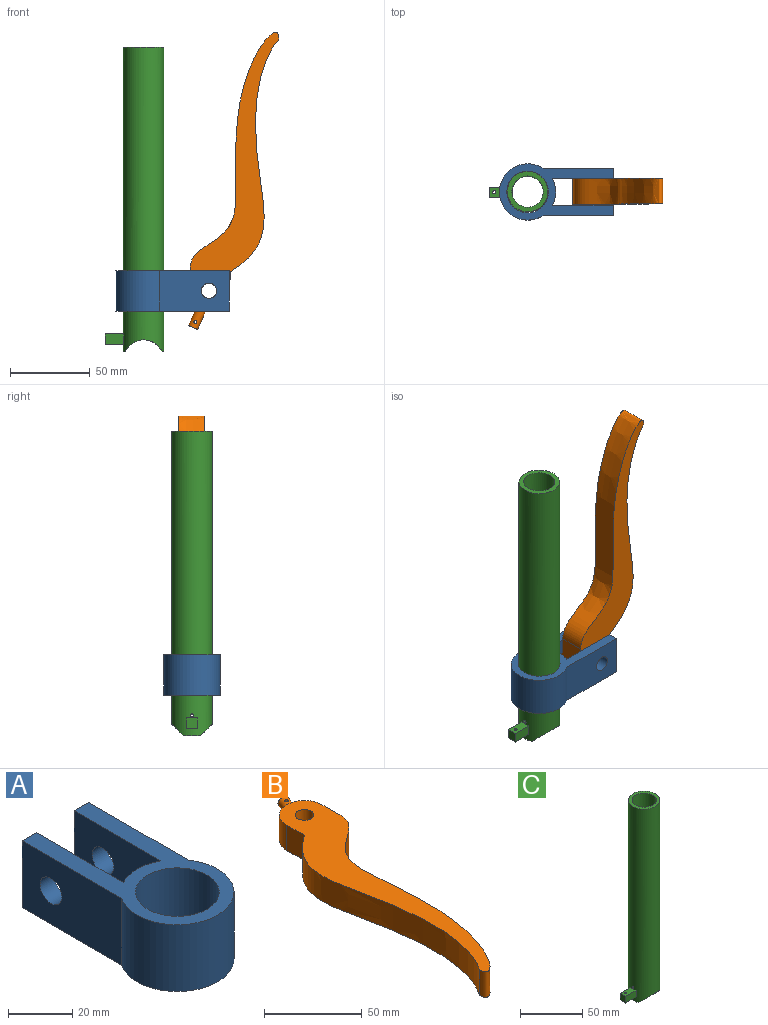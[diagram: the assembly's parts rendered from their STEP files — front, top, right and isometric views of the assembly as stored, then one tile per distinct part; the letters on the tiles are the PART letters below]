
ASSEMBLY  parts=3 mates=2
PART A: 13 faces, bbox 35.2x71.2x25.4 mm
  f0: plane 38.1x25.4mm, normal (-1,0,0), area 896.5mm2, adj f1,f7,f9,f10,f11
  f1: cylinder r=17.59mm len=25.4mm, axis (0,0,-1), area 436.5mm2, adj f0,f2,f9,f10
  f2: plane 38.1x25.4mm, normal (1,0,0), area 896.5mm2, adj f1,f3,f9,f10,f12
  f3: plane 25.4x6.35mm, normal (0,1,0), area 161.3mm2, adj f2,f4,f9,f10
  f4: plane 43.83x25.4mm, normal (-1,0,0), area 1042mm2, adj f3,f5,f9,f10,f12
  f5: cylinder r=17.59mm len=35.18mm, axis (0,0,-1), area 1931.8mm2, adj f4,f6,f9,f10
  f6: plane 43.83x25.4mm, normal (1,0,0), area 1042mm2, adj f5,f7,f9,f10,f11
  f7: plane 25.4x6.35mm, normal (0,1,0), area 161.3mm2, adj f0,f6,f9,f10
  f8: cylinder r=13.02mm len=26.04mm, axis (0,0,-1), area 2077.5mm2, adj f9,f10
  f9: plane 71.22x35.18mm, normal (0,0,1), area 953.8mm2, adj f0,f1,f2,f3,f4,f5,f6,f7
  f10: plane 71.22x35.18mm, normal (0,0,-1), area 953.8mm2, adj f0,f1,f2,f3,f4,f5,f6,f7
  f11: cylinder r=4.76mm len=9.53mm, axis (-1,0,0), area 190mm2, adj f0,f6
  f12: cylinder r=4.76mm len=9.53mm, axis (-1,0,0), area 190mm2, adj f2,f4
PART B: 11 faces, bbox 57.1x193.9x15.9 mm
  f0: plane 6.35x5.97mm, normal (0.34,0.94,0), area 31.7mm2, adj f9
  f1: plane 182x57.15mm, normal (0,0,1), area 2823.6mm2, adj f3,f4,f5,f6,f7,f8
  f2: plane 182x57.15mm, normal (0,0,-1), area 2823.6mm2, adj f3,f4,f5,f6,f7,f8
  f3: extruded ~151.31x46.5mm, area 2736.8mm2, adj f1,f2,f4,f7
  f4: plane 15.88x12.7mm, normal (1,0,0), area 201.6mm2, adj f1,f2,f3,f5
  f5: cylinder r=12.7mm len=25.4mm, axis (0,0,-1), area 601.5mm2, adj f1,f2,f4,f6,f9
  f6: plane 15.88x12.7mm, normal (-1,0,0), area 201.6mm2, adj f1,f2,f5,f7
  f7: extruded ~147.26x21.1mm, area 2495.1mm2, adj f1,f2,f3,f6
  f8: cylinder r=4.76mm len=15.88mm, axis (0,0,-1), area 475mm2, adj f1,f2
  f9: cylinder r=3.17mm len=14.11mm, axis (0.34,0.94,0), area 243.4mm2, adj f0,f5,f10
  f10: cylinder r=0.97mm len=6.35mm, axis (0,0,-1), area 37.6mm2, adj f9
PART C: 17 faces, bbox 36.8x25.4x190.5 mm
  f0: cylinder r=12.7mm len=190.5mm, axis (0,0,-1), area 14874.6mm2, adj f1,f2,f4,f5,f6,f7,f11,f12
  f1: plane 10.58x1.15mm, normal (0,0,-1), area 8.2mm2, adj f0,f5
  f2: plane 25.4x25.4mm, normal (0,0,1), area 206.3mm2, adj f0,f3
  f3: cylinder r=9.78mm len=187.69mm, axis (0,0,1), area 11348.8mm2, adj f2,f5,f6,f7,f8,f9,f10
  f4: plane 10.58x1.15mm, normal (0,0,-1), area 8.2mm2, adj f0,f5
  f5: cylinder r=12.7mm len=25.45mm, axis (0,-1,0), area 256.3mm2, adj f0,f1,f3,f4
  f6: cylinder r=0.97mm len=2.97mm, axis (1,0,0), area 17.7mm2, adj f0,f3
  f7: cylinder r=0.97mm len=2.97mm, axis (1,0,0), area 17.7mm2, adj f0,f3
  f8: plane 6.35x4.43mm, normal (1,0,0), area 28.1mm2, adj f3,f9,f10
  f9: plane 4.43x0.25mm, normal (0,0,1), area 0.8mm2, adj f3,f8
  f10: plane 4.43x0.25mm, normal (0,0,-1), area 0.8mm2, adj f3,f8
  f11: plane 11.83x6.35mm, normal (0,1,0), area 75.1mm2, adj f0,f13,f14,f15
  f12: plane 11.83x6.35mm, normal (0,-1,0), area 75.1mm2, adj f0,f13,f14,f15
  f13: plane 11.83x6.35mm, normal (0,0,-1), area 70.5mm2, adj f0,f11,f12,f15,f16
  f14: plane 11.83x6.35mm, normal (0,0,1), area 70.5mm2, adj f0,f11,f12,f15,f16
  f15: plane 6.35x6.35mm, normal (-1,0,0), area 40.3mm2, adj f11,f12,f13,f14
  f16: cylinder r=0.97mm len=6.35mm, axis (0,0,1), area 38.5mm2, adj f13,f14
PLACE A rot(axis=(0.71,0.71,0),180deg) t=(10.46,53.29,66.91)mm
PLACE B rot(axis=(0.02,-0.71,0.71),177.5deg) t=(69.66,66.3,142.14)mm
PLACE C t=(10.46,24.71,16.11)mm fixed
MATE revolute B.f5 <-> A.f11  axis (0,1,0) through (51.39,61.54,54.21)mm
MATE fastened A.f8 <-> C.f0  axis (0,0,1) through (10.46,53.29,54.21)mm
